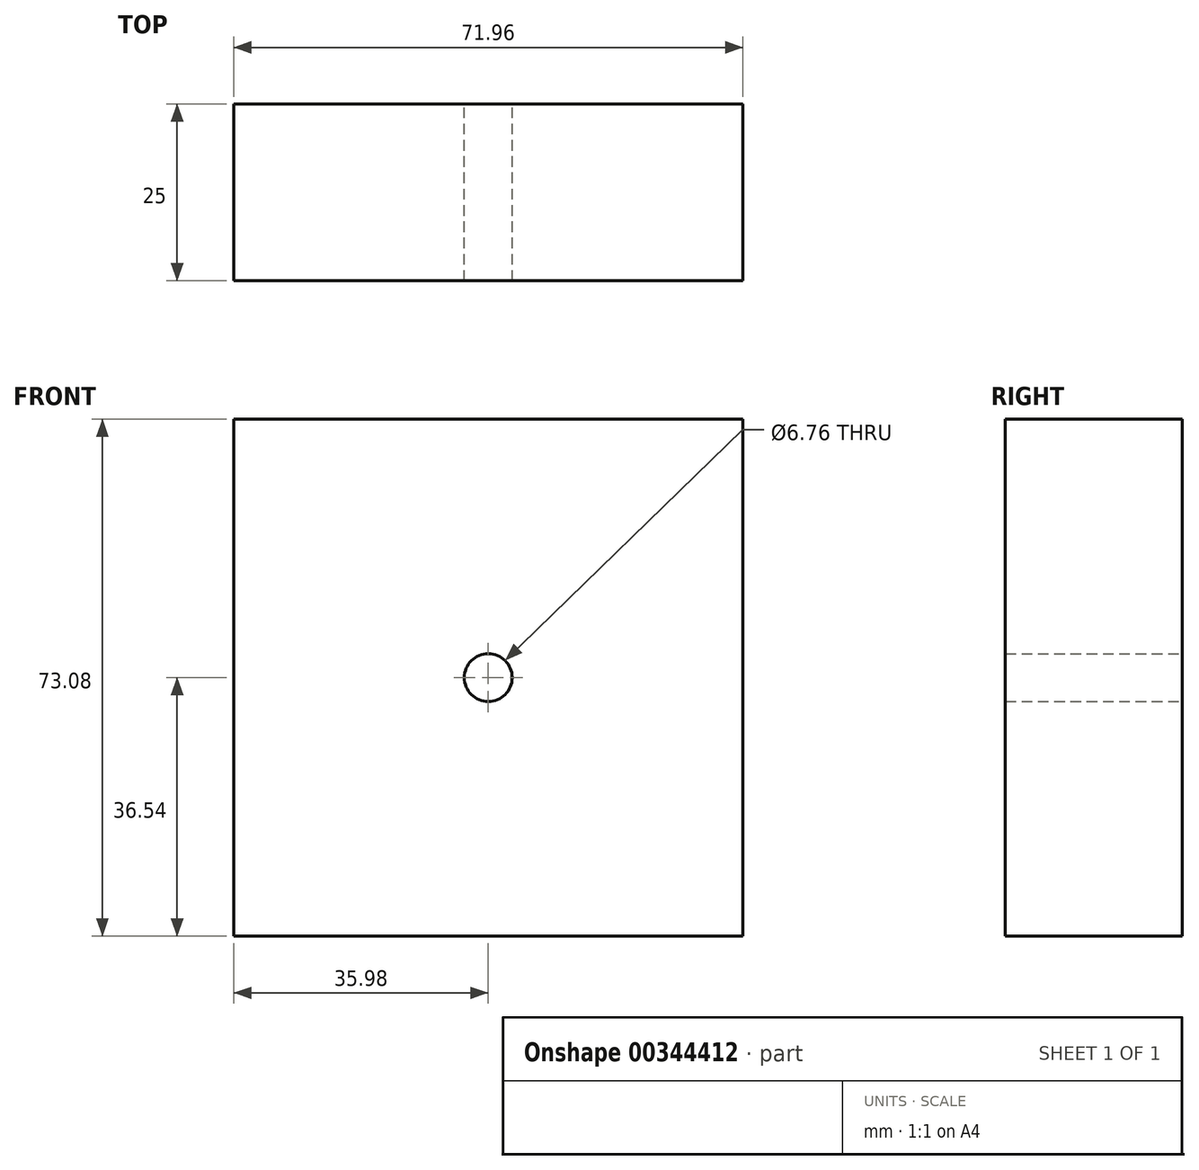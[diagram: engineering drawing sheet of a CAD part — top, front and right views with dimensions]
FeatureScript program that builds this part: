
annotation { "Feature Type Name" : "Feature", "Feature Type Description" : "" }
export const myFeature = defineFeature(function(context is Context, id is Id, definition is map)
    precondition{}
    {
        {
            var Q0;
            Q0=qCreatedBy(makeId("Front.planeOp"),FACE);
            var sketch = newSketch(context, id + "F0", { "sketchPlane" : qUnion([Q0])});
            skLineSegment(sketch, "E0.bottom", {"start": v(-35.98, -36.54) * mm, "end": v(35.98, -36.54) * mm});
            skLineSegment(sketch, "E0.top", {"start": v(-35.98, 36.54) * mm, "end": v(35.98, 36.54) * mm});
            skLineSegment(sketch, "E0.left", {"start": v(-35.98, -36.54) * mm, "end": v(-35.98, 36.54) * mm});
            skLineSegment(sketch, "E0.right", {"start": v(35.98, -36.54) * mm, "end": v(35.98, 36.54) * mm});
            skPoint(sketch, "E0.middle", {"position": v(0, 0) * mm});
            skSolve(sketch);
        }
        {
            var Q0;
            Q0=makeQuery(id+"F0.imprint","IMPRINT",FACE,{"disambiguationData":[TD([[makeQuery(id+"F0.imprint","IMPRINT",EDGE,{"derivedFrom":sQuery(id+"F0.wireOp",EDGE,"E0.bottom")}),1.0]])]});
            extrude(context, id + "F1", {"entities" : qUnion([Q0]), "depth" : 25 * mm});
        }
        {
            var Q0;
            Q0=makeQuery(id+"F1.opExtrude","CAP_FACE",FACE,{"disambiguationData":[OSD([sQuery(id+"F0.wireOp",EDGE,"E0.bottom"),sQuery(id+"F0.wireOp",EDGE,"E0.top"),sQuery(id+"F0.wireOp",EDGE,"E0.left"),sQuery(id+"F0.wireOp",EDGE,"E0.right")])],"isStart":true});
            var sketch = newSketch(context, id + "F2", { "sketchPlane" : qUnion([Q0])});
            skPoint(sketch, "E1", {"position": v(0, 0) * mm});
            skSolve(sketch);
        }
        {
            var Q0;
            Q0=sQuery(id+"F2.wireOp",VERTEX,"E1");
            var Q1;
            Q1=makeQuery(id+"F1.opExtrude","SWEPT_BODY",BODY,{"disambiguationData":[OSD([sQuery(id+"F0.wireOp",EDGE,"E0.bottom"),sQuery(id+"F0.wireOp",EDGE,"E0.top"),sQuery(id+"F0.wireOp",EDGE,"E0.left"),sQuery(id+"F0.wireOp",EDGE,"E0.right")])]});
            hole(context, id + "F3", {"style" : HoleStyle.SIMPLE, "endStyle" : HoleEndStyle.THROUGH, "standardTappedOrClearance" : lookupTablePath({ "standard" : "ANSI", "fit" : "Normal (ASME)", "size" : "1/4", "type" : "Clearance" }), "standardBlindInLast" : lookupTablePath({ "fit" : "Free", "standard" : "ANSI", "size" : "1/4", "type" : "Clearance" }), "holeDiameter" : 6.76 * mm, "isTappedThrough" : true, "tappedDepth" : 12 * mm, "tapClearance" : 3, "locations" : qUnion([Q0]), "scope" : qUnion([Q1])});
        }
    });
